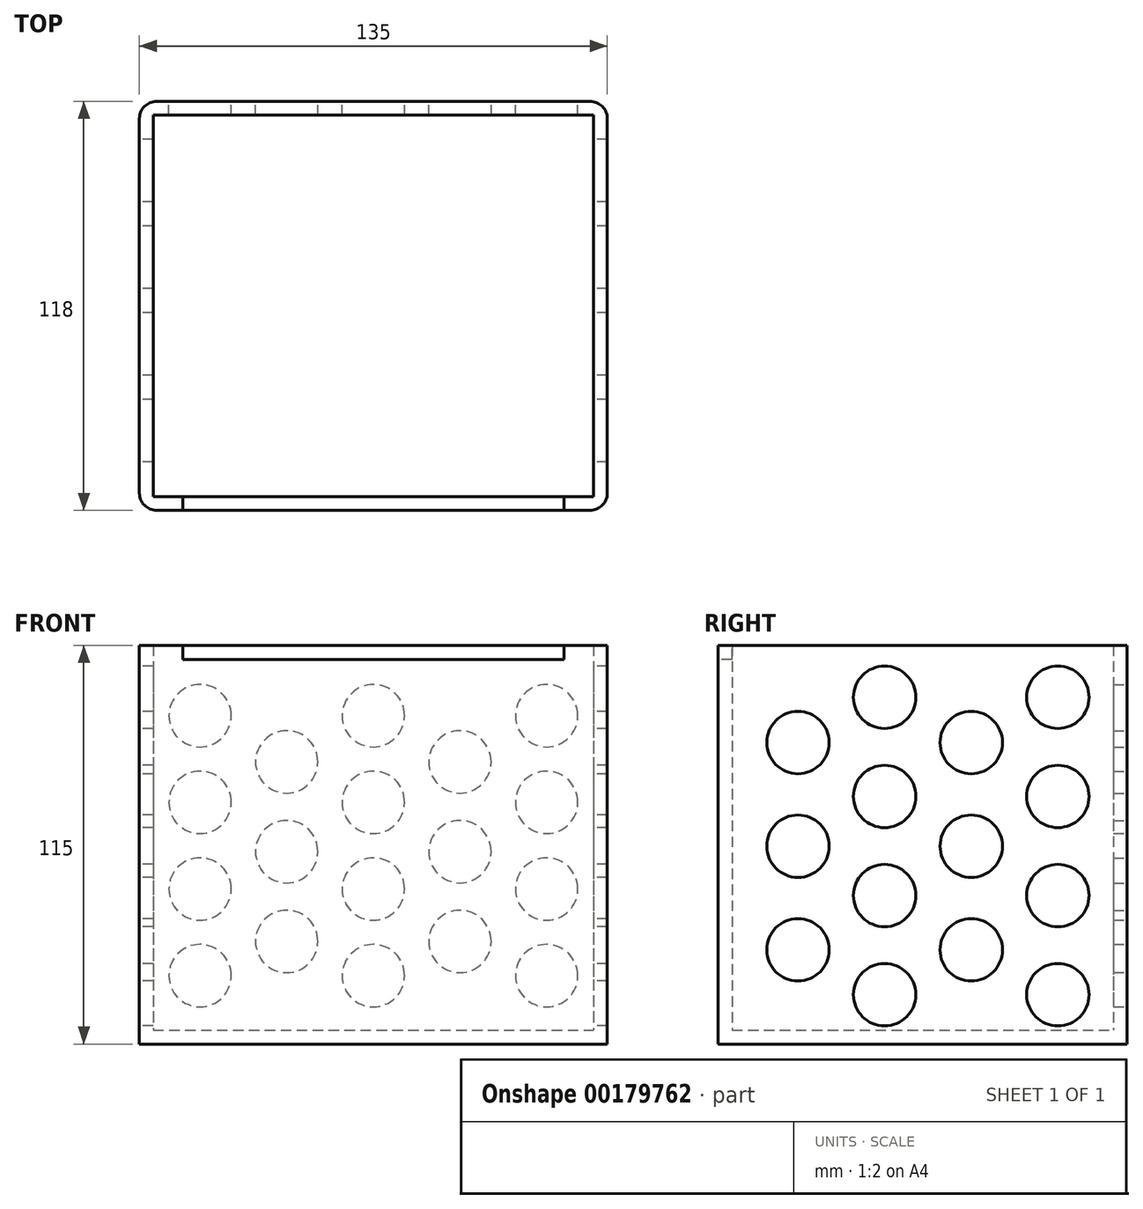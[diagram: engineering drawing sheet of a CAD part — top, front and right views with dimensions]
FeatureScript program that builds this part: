
annotation { "Feature Type Name" : "Feature", "Feature Type Description" : "" }
export const myFeature = defineFeature(function(context is Context, id is Id, definition is map)
    precondition{}
    {
        {
            var Q0;
            Q0=qCreatedBy(makeId("Top.planeOp"),FACE);
            var sketch = newSketch(context, id + "F0", { "sketchPlane" : qUnion([Q0])});
            skLineSegment(sketch, "E0.bottom", {"start": v(0, 0) * mm, "end": v(127, 0) * mm});
            skLineSegment(sketch, "E0.top", {"start": v(0, 110) * mm, "end": v(127, 110) * mm});
            skLineSegment(sketch, "E0.left", {"start": v(0, 0) * mm, "end": v(0, 110) * mm});
            skLineSegment(sketch, "E0.right", {"start": v(127, 0) * mm, "end": v(127, 110) * mm});
            skLineSegment(sketch, "E1.0", {"start": v(131, -4) * mm, "end": v(131, 114) * mm});
            skLineSegment(sketch, "E1.1", {"start": v(-4, -4) * mm, "end": v(131, -4) * mm});
            skLineSegment(sketch, "E1.2", {"start": v(-4, -4) * mm, "end": v(-4, 114) * mm});
            skLineSegment(sketch, "E1.3", {"start": v(-4, 114) * mm, "end": v(131, 114) * mm});
            skSolve(sketch);
        }
        {
            var Q0;
            Q0 = qSketchRegion(id + "F0", true);
            extrude(context, id + "F1", {"entities" : qUnion([Q0]), "depth" : 115 * mm});
        }
        {
            var Q0;
            Q0=makeQuery(id+"F0.imprint","IMPRINT",FACE,{"disambiguationData":[TD([[makeQuery(id+"F0.imprint","IMPRINT",EDGE,{"derivedFrom":sQuery(id+"F0.wireOp",EDGE,"E0.bottom")}),1.0]])]});
            extrude(context, id + "F11", {"entities" : qUnion([Q0]), "operationType" : NewBodyOperationType.ADD, "depth" : 4 * mm});
        }
        {
            var Q0;
            Q0=makeQuery(id+"F1.opExtrude","SWEPT_FACE",FACE,{"disambiguationData":[OSD([sQuery(id+"F0.wireOp",EDGE,"E1.1")])]});
            var sketch = newSketch(context, id + "F2", { "sketchPlane" : qUnion([Q0])});
            skLineSegment(sketch, "E2.0", {"start": v(0, 111) * mm, "end": v(127, 111) * mm});
            skLineSegment(sketch, "E2.1", {"start": v(0, 111) * mm, "end": v(0, 4) * mm});
            skLineSegment(sketch, "E2.2", {"start": v(0, 4) * mm, "end": v(127, 4) * mm});
            skLineSegment(sketch, "E2.3", {"start": v(127, 111) * mm, "end": v(127, 4) * mm});
            skLineSegment(sketch, "E3", {"start": v(63.5, 4) * mm, "end": v(63.5, 111) * mm, "construction": true});
            skLineSegment(sketch, "E4", {"start": v(118.52, 115) * mm, "end": v(118.52, 96.08) * mm});
            skFitSpline(sketch, "E5", {"points": [v(118.52, 96.08) * mm, v(110.13, 86.14) * mm, v(99.72, 90.02) * mm, v(99.72, 90.02) * mm, v(93.33, 79.14) * mm, v(79.58, 80.4) * mm, v(63.5, 69.67) * mm], "startDerivative": vector(-1.02, -146.81) * mm, "endDerivative": vector(-46.7, -127.35) * mm});
            skFitSpline(sketch, "E6.MirrorCS", {"points": [v(8.48, 96.08) * mm, v(16.87, 86.14) * mm, v(27.28, 90.02) * mm, v(27.28, 90.02) * mm, v(33.67, 79.14) * mm, v(47.42, 80.4) * mm, v(63.5, 69.67) * mm], "startDerivative": vector(1.02, -146.81) * mm, "endDerivative": vector(46.7, -127.35) * mm});
            skLineSegment(sketch, "E7.MirrorCS", {"start": v(8.48, 115) * mm, "end": v(8.48, 96.08) * mm});
            skSolve(sketch);
        }
        {
            var Q0;
            {var subQ0=sQuery(id+"F2.wireOp",EDGE,"E5");Q0=makeQuery(id+"F2.imprint","IMPRINT",FACE,{"disambiguationData":[TD([[makeQuery(id+"F2.imprint","IMPRINT",EDGE,{"derivedFrom":subQ0}),-1.0]])]});}
            var Q1;
            {var subQ0=sQuery(id+"F2.wireOp",EDGE,"E7.MirrorCS");var subQ1=sQuery(id+"F2.wireOp",EDGE,"E2.0");var subQ2=makeQuery(id+"F2.imprint","INTERSECT",VERTEX,{"derivedFrom":[subQ1,subQ0]});Q1=makeQuery(id+"F2.imprint","IMPRINT",FACE,{"disambiguationData":[TD([[makeQuery(id+"F2.imprint","IMPRINT",EDGE,{"disambiguationData":[TD([[subQ2,-1.0]])],"derivedFrom":subQ1}),1.0]])]});}
            extrude(context, id + "F3", {"entities" : qUnion([Q0, Q1]), "operationType" : NewBodyOperationType.REMOVE, "oppositeDirection" : true, "depth" : 25 * mm});
        }
        {
            var Q0;
            Q0=makeQuery(id+"F1.opExtrude","SWEPT_FACE",FACE,{"disambiguationData":[OSD([sQuery(id+"F0.wireOp",EDGE,"E1.2")])]});
            var sketch = newSketch(context, id + "F4", { "sketchPlane" : qUnion([Q0])});
            skLineSegment(sketch, "E8.0", {"start": v(-94, 115) * mm, "end": v(-94, 0) * mm});
            skLineSegment(sketch, "E9.1.0.0", {"start": v(-69, 115) * mm, "end": v(-69, 0) * mm});
            skLineSegment(sketch, "E9.2.0.0", {"start": v(-44, 115) * mm, "end": v(-44, 0) * mm});
            skLineSegment(sketch, "E9.3.0.0", {"start": v(-19, 115) * mm, "end": v(-19, 0) * mm});
            skLineSegment(sketch, "E9.direction1", {"start": v(-94, 0) * mm, "end": v(-69, 0) * mm, "construction": true});
            skCircle(sketch, "E10", {"center": v(-94, 100.05) * mm, "radius": 9 * mm});
            skCircle(sketch, "E11.0.1.0", {"center": v(-94, 71.45) * mm, "radius": 9 * mm});
            skCircle(sketch, "E11.0.2.0", {"center": v(-94, 42.85) * mm, "radius": 9 * mm});
            skCircle(sketch, "E11.0.3.0", {"center": v(-94, 14.25) * mm, "radius": 9 * mm});
            skLineSegment(sketch, "E11.direction1", {"start": v(-94, 100.05) * mm, "end": v(-68.4, 100.05) * mm, "construction": true});
            skLineSegment(sketch, "E11.direction2", {"start": v(-94, 100.05) * mm, "end": v(-94, 71.45) * mm, "construction": true});
            skCircle(sketch, "E12", {"center": v(-69, 27.19) * mm, "radius": 9 * mm});
            skCircle(sketch, "E13.0.1.0", {"center": v(-69, 57.09) * mm, "radius": 9 * mm});
            skCircle(sketch, "E13.0.2.0", {"center": v(-69, 86.99) * mm, "radius": 9 * mm});
            skCircle(sketch, "E13.1.0.0", {"center": v(-19, 27.19) * mm, "radius": 9 * mm});
            skCircle(sketch, "E13.1.1.0", {"center": v(-19, 57.09) * mm, "radius": 9 * mm});
            skCircle(sketch, "E13.1.2.0", {"center": v(-19, 86.99) * mm, "radius": 9 * mm});
            skLineSegment(sketch, "E13.direction1", {"start": v(-69, 27.19) * mm, "end": v(-19, 27.19) * mm, "construction": true});
            skLineSegment(sketch, "E13.direction2", {"start": v(-69, 27.19) * mm, "end": v(-69, 57.09) * mm, "construction": true});
            skCircle(sketch, "E14.1.0.0", {"center": v(-44, 100.05) * mm, "radius": 9 * mm});
            skCircle(sketch, "E14.1.0.1", {"center": v(-44, 71.45) * mm, "radius": 9 * mm});
            skCircle(sketch, "E14.1.0.2", {"center": v(-44, 42.85) * mm, "radius": 9 * mm});
            skCircle(sketch, "E14.1.0.3", {"center": v(-44, 14.25) * mm, "radius": 9 * mm});
            skLineSegment(sketch, "E14.direction1", {"start": v(-94, 100.05) * mm, "end": v(-44, 100.05) * mm, "construction": true});
            skSolve(sketch);
        }
        {
            var Q0;
            Q0 = qSketchRegion(id + "F4", true);
            extrude(context, id + "F5", {"entities" : qUnion([Q0]), "operationType" : NewBodyOperationType.REMOVE, "endBound" : BoundingType.THROUGH_ALL, "oppositeDirection" : true, "depth" : 25 * mm});
        }
        {
            var Q0;
            Q0=makeQuery(id+"F1.opExtrude","SWEPT_FACE",FACE,{"disambiguationData":[OSD([sQuery(id+"F0.wireOp",EDGE,"E1.3")])]});
            var sketch = newSketch(context, id + "F6", { "sketchPlane" : qUnion([Q0])});
            skLineSegment(sketch, "E15", {"start": v(-63.5, 115) * mm, "end": v(-63.5, 0) * mm, "construction": true});
            skLineSegment(sketch, "E16.1.0.0", {"start": v(-38.5, 115) * mm, "end": v(-38.5, 0) * mm, "construction": true});
            skLineSegment(sketch, "E16.2.0.0", {"start": v(-13.5, 115) * mm, "end": v(-13.5, 0) * mm, "construction": true});
            skLineSegment(sketch, "E16.direction1", {"start": v(-63.5, 0) * mm, "end": v(-38.5, 0) * mm, "construction": true});
            skLineSegment(sketch, "E17.1.0.0", {"start": v(-88.5, 115) * mm, "end": v(-88.5, 0) * mm, "construction": true});
            skLineSegment(sketch, "E17.2.0.0", {"start": v(-113.5, 115) * mm, "end": v(-113.5, 0) * mm, "construction": true});
            skLineSegment(sketch, "E17.direction1", {"start": v(-63.5, 0) * mm, "end": v(-88.5, 0) * mm, "construction": true});
            skCircle(sketch, "E18", {"center": v(-113.5, 94.74) * mm, "radius": 9 * mm});
            skCircle(sketch, "E19.0.1.0", {"center": v(-113.5, 69.74) * mm, "radius": 9 * mm});
            skCircle(sketch, "E19.0.2.0", {"center": v(-113.5, 44.74) * mm, "radius": 9 * mm});
            skCircle(sketch, "E19.0.3.0", {"center": v(-113.5, 19.74) * mm, "radius": 9 * mm});
            skCircle(sketch, "E19.1.0.0", {"center": v(-63.5, 94.74) * mm, "radius": 9 * mm});
            skCircle(sketch, "E19.1.1.0", {"center": v(-63.5, 69.74) * mm, "radius": 9 * mm});
            skCircle(sketch, "E19.1.2.0", {"center": v(-63.5, 44.74) * mm, "radius": 9 * mm});
            skCircle(sketch, "E19.1.3.0", {"center": v(-63.5, 19.74) * mm, "radius": 9 * mm});
            skCircle(sketch, "E19.2.0.0", {"center": v(-13.5, 94.74) * mm, "radius": 9 * mm});
            skCircle(sketch, "E19.2.1.0", {"center": v(-13.5, 69.74) * mm, "radius": 9 * mm});
            skCircle(sketch, "E19.2.2.0", {"center": v(-13.5, 44.74) * mm, "radius": 9 * mm});
            skCircle(sketch, "E19.2.3.0", {"center": v(-13.5, 19.74) * mm, "radius": 9 * mm});
            skLineSegment(sketch, "E19.direction1", {"start": v(-113.5, 94.74) * mm, "end": v(-63.5, 94.74) * mm, "construction": true});
            skLineSegment(sketch, "E19.direction2", {"start": v(-113.5, 94.74) * mm, "end": v(-113.5, 69.74) * mm, "construction": true});
            skCircle(sketch, "E20", {"center": v(-88.5, 81.4) * mm, "radius": 9 * mm});
            skCircle(sketch, "E21.0.1.0", {"center": v(-88.5, 55.5) * mm, "radius": 9 * mm});
            skCircle(sketch, "E21.0.2.0", {"center": v(-88.5, 29.6) * mm, "radius": 9 * mm});
            skCircle(sketch, "E21.1.0.0", {"center": v(-38.5, 81.4) * mm, "radius": 9 * mm});
            skCircle(sketch, "E21.1.1.0", {"center": v(-38.5, 55.5) * mm, "radius": 9 * mm});
            skCircle(sketch, "E21.1.2.0", {"center": v(-38.5, 29.6) * mm, "radius": 9 * mm});
            skLineSegment(sketch, "E21.direction1", {"start": v(-88.5, 81.4) * mm, "end": v(-38.5, 81.4) * mm, "construction": true});
            skLineSegment(sketch, "E21.direction2", {"start": v(-88.5, 81.4) * mm, "end": v(-88.5, 55.5) * mm, "construction": true});
            skSolve(sketch);
        }
        {
            var Q0;
            Q0 = qSketchRegion(id + "F6", true);
            extrude(context, id + "F7", {"entities" : qUnion([Q0]), "operationType" : NewBodyOperationType.REMOVE, "oppositeDirection" : true, "depth" : 25 * mm});
        }
        {
            var Q0;
            Q0=makeQuery(id+"F1.opExtrude","SWEPT_EDGE",EDGE,{"disambiguationData":[OSD([sQuery(id+"F0.wireOp",EDGE,"E1.2"),sQuery(id+"F0.wireOp",EDGE,"E1.3")])]});
            var Q1;
            Q1=makeQuery(id+"F1.opExtrude","SWEPT_EDGE",EDGE,{"disambiguationData":[OSD([sQuery(id+"F0.wireOp",EDGE,"E1.0"),sQuery(id+"F0.wireOp",EDGE,"E1.3")])]});
            var Q2;
            Q2=makeQuery(id+"F1.opExtrude","SWEPT_EDGE",EDGE,{"disambiguationData":[OSD([sQuery(id+"F0.wireOp",EDGE,"E1.0"),sQuery(id+"F0.wireOp",EDGE,"E1.1")])]});
            var Q3;
            Q3=makeQuery(id+"F1.opExtrude","SWEPT_EDGE",EDGE,{"disambiguationData":[OSD([sQuery(id+"F0.wireOp",EDGE,"E1.1"),sQuery(id+"F0.wireOp",EDGE,"E1.2")])]});
            var Q4;
            Q4=makeQuery(id+"F3.boolean.opBoolean","COPY",EDGE,{"derivedFrom":makeQuery(id+"F3.opExtrude","SWEPT_EDGE",EDGE,{"disambiguationData":[OSD([sQuery(id+"F0.wireOp",EDGE,"E1.1"),sQuery(id+"F2.wireOp",EDGE,"E7.MirrorCS")])]})});
            var Q5;
            Q5=makeQuery(id+"F3.boolean.opBoolean","COPY",EDGE,{"derivedFrom":makeQuery(id+"F3.opExtrude","SWEPT_EDGE",EDGE,{"disambiguationData":[OSD([sQuery(id+"F0.wireOp",EDGE,"E1.1"),sQuery(id+"F2.wireOp",EDGE,"E4")])]})});
            fillet(context, id + "F8", {"entities" : qUnion([Q0, Q1, Q2, Q3, Q4, Q5]), "radius" : 5 * mm, "tangentPropagation" : true, "allowEdgeOverflow" : false});
        }
    });
